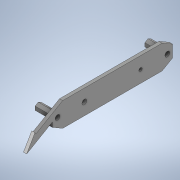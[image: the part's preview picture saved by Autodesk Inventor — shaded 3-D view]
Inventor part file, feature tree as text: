
AUTODESK INVENTOR PART (.ipt)
format: ipt  version: 2020 (Build 240168000, 168)  size: 165,888 bytes
history: native  units: in
note: dims shown in document units (in); Inventor stores cm internally (conversion verified against a paired STEP export)
features: other x3, extrude x1, sketch x1
ambient origin geometry x8: Origin, YZ Plane, XZ Plane, XY Plane, X Axis, Y Axis, Z Axis, Center Point
bodies: Solid1 (feature_tree)
feature tree (5):
  other  "HexWheelGuard.ipt"
  extrude  "Extrusion1"  Depth=0.315in
  other  "Solid1::HexWheelGuard.ipt"
  other  "TaggingFeature2"
  sketch  "Sketch1"  dims[d1=0.3937in d2=0.315in d3=60.0deg d4=1.3858in d5=0.0787in d6=0.3937in d7=0.0in]
